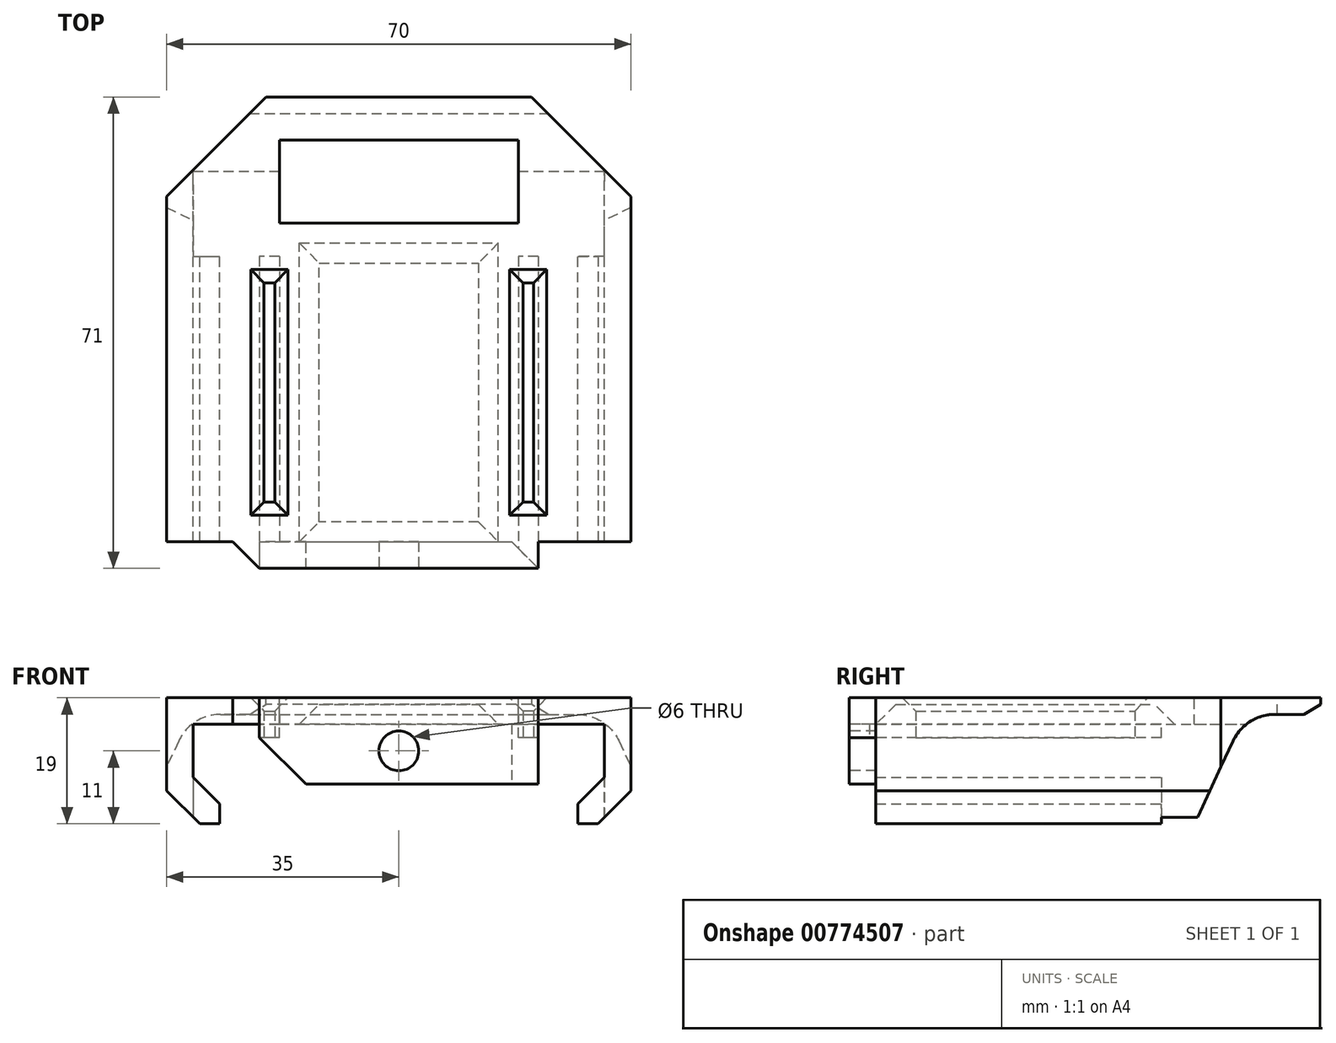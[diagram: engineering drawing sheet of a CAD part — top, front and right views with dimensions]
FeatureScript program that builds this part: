
annotation { "Feature Type Name" : "Feature", "Feature Type Description" : "" }
export const myFeature = defineFeature(function(context is Context, id is Id, definition is map)
    precondition{}
    {
        {
            var Q0;
            Q0=qCreatedBy(makeId("Front.planeOp"),FACE);
            var sketch = newSketch(context, id + "F0", { "sketchPlane" : qUnion([Q0])});
            skLineSegment(sketch, "E0.bottom", {"start": v(-35, 0) * mm, "end": v(35, 0) * mm});
            skLineSegment(sketch, "E0.top", {"start": v(-35, -19) * mm, "end": v(-27, -19) * mm});
            skLineSegment(sketch, "E0.left", {"start": v(-35, 0) * mm, "end": v(-35, -19) * mm});
            skLineSegment(sketch, "E0.right", {"start": v(35, 0) * mm, "end": v(35, -19) * mm});
            skLineSegment(sketch, "E1", {"start": v(-27, -19) * mm, "end": v(-27, -16) * mm});
            skLineSegment(sketch, "E2", {"start": v(-31, -12) * mm, "end": v(-31, -4) * mm});
            skLineSegment(sketch, "E3", {"start": v(-31, -4) * mm, "end": v(31, -4) * mm});
            skLineSegment(sketch, "E4", {"start": v(31, -4) * mm, "end": v(31, -12) * mm});
            skLineSegment(sketch, "E5", {"start": v(27, -16) * mm, "end": v(27, -19) * mm});
            skLineSegment(sketch, "E6.trimOffspring", {"start": v(27, -19) * mm, "end": v(35, -19) * mm});
            skPoint(sketch, "E7.startSnap0", {"position": v(-29, -12) * mm});
            skLineSegment(sketch, "E8", {"start": v(-31, -12) * mm, "end": v(-27, -16) * mm});
            skLineSegment(sketch, "E9", {"start": v(31, -12) * mm, "end": v(27, -16) * mm});
            skPoint(sketch, "E10.orphan", {"position": v(-27, -12) * mm});
            skSolve(sketch);
        }
        {
            var Q0;
            Q0 = qSketchRegion(id + "F0", true);
            extrude(context, id + "F1", {"entities" : qUnion([Q0]), "depth" : 67 * mm, "offsetDistance" : 25 * mm});
        }
        {
            var Q0;
            Q0=makeQuery(id+"F1.opExtrude","SWEPT_FACE",FACE,{"disambiguationData":[OSD([sQuery(id+"F0.wireOp",EDGE,"E0.right")])]});
            var sketch = newSketch(context, id + "F2", { "sketchPlane" : qUnion([Q0])});
            skLineSegment(sketch, "E11.0.1", {"start": v(0, -4) * mm, "end": v(-67, -4) * mm, "construction": true});
            skLineSegment(sketch, "E11.0.3", {"start": v(-67, -4) * mm, "end": v(0, -4) * mm, "construction": true});
            skLineSegment(sketch, "E12", {"start": v(-19, -19) * mm, "end": v(-13.2, -6.54) * mm});
            skLineSegment(sketch, "E13", {"start": v(-6.85, -2.5) * mm, "end": v(4.14, -2.5) * mm});
            skLineSegment(sketch, "E14", {"start": v(4.14, -2.5) * mm, "end": v(4.14, -19) * mm});
            skLineSegment(sketch, "E15", {"start": v(4.14, -19) * mm, "end": v(-19, -19) * mm});
            skPoint(sketch, "E16.visualSharp", {"position": v(-11.3, -2.5) * mm});
            skArc(sketch, "E16.filletArc", {"start": v(-6.85, -2.5) * mm, "mid": v(-10.6, -3.6) * mm, "end": v(-13.2, -6.54) * mm});
            skSolve(sketch);
        }
        {
            var Q0;
            Q0 = qSketchRegion(id + "F2", true);
            extrude(context, id + "F3", {"entities" : qUnion([Q0]), "operationType" : NewBodyOperationType.REMOVE, "endBound" : BoundingType.THROUGH_ALL, "oppositeDirection" : true, "depth" : 25 * mm, "offsetDistance" : 25 * mm});
        }
        {
            var Q0;
            Q0=makeQuery(id+"F1.opExtrude","SWEPT_FACE",FACE,{"disambiguationData":[OSD([sQuery(id+"F0.wireOp",EDGE,"E0.bottom")])]});
            var sketch = newSketch(context, id + "F4", { "sketchPlane" : qUnion([Q0])});
            skLineSegment(sketch, "E17.bottom", {"start": v(18, -19) * mm, "end": v(-18, -19) * mm});
            skLineSegment(sketch, "E17.top", {"start": v(18, -6.5) * mm, "end": v(-18, -6.5) * mm});
            skLineSegment(sketch, "E17.left", {"start": v(18, -19) * mm, "end": v(18, -6.5) * mm});
            skLineSegment(sketch, "E17.right", {"start": v(-18, -19) * mm, "end": v(-18, -6.5) * mm});
            skPoint(sketch, "E17.middle", {"position": v(0, -12.75) * mm});
            skSolve(sketch);
        }
        {
            var Q0;
            Q0 = qSketchRegion(id + "F4", true);
            extrude(context, id + "F5", {"entities" : qUnion([Q0]), "operationType" : NewBodyOperationType.REMOVE, "oppositeDirection" : true, "depth" : 25 * mm, "offsetDistance" : 25 * mm});
        }
        {
            var Q0;
            Q0=makeQuery(id+"F1.opExtrude","SWEPT_FACE",FACE,{"disambiguationData":[OSD([sQuery(id+"F0.wireOp",EDGE,"E3")])]});
            var sketch = newSketch(context, id + "F6", { "sketchPlane" : qUnion([Q0])});
            skLineSegment(sketch, "E18.bottom", {"start": v(-18, 24) * mm, "end": v(-21, 24) * mm});
            skLineSegment(sketch, "E18.top", {"start": v(-18, 67) * mm, "end": v(-21, 67) * mm});
            skLineSegment(sketch, "E18.left", {"start": v(-18, 24) * mm, "end": v(-18, 67) * mm});
            skLineSegment(sketch, "E18.right", {"start": v(-21, 24) * mm, "end": v(-21, 67) * mm});
            skPoint(sketch, "E18.middle", {"position": v(-19.5, 45.5) * mm});
            skLineSegment(sketch, "E19.bottom", {"start": v(21, 24) * mm, "end": v(18, 24) * mm});
            skLineSegment(sketch, "E19.top", {"start": v(21, 67) * mm, "end": v(18, 67) * mm});
            skLineSegment(sketch, "E19.left", {"start": v(21, 24) * mm, "end": v(21, 67) * mm});
            skLineSegment(sketch, "E19.right", {"start": v(18, 24) * mm, "end": v(18, 67) * mm});
            skPoint(sketch, "E19.middle", {"position": v(19.5, 45.5) * mm});
            skSolve(sketch);
        }
        {
            var Q0;
            Q0 = qSketchRegion(id + "F6", true);
            extrude(context, id + "F7", {"entities" : qUnion([Q0]), "operationType" : NewBodyOperationType.ADD, "depth" : 2 * mm, "offsetDistance" : 25 * mm});
        }
        {
            var Q0;
            Q0=makeQuery(id+"F7.opExtrude","CAP_FACE",FACE,{"disambiguationData":[OSD([sQuery(id+"F6.wireOp",EDGE,"E18.bottom"),sQuery(id+"F6.wireOp",EDGE,"E18.top"),sQuery(id+"F6.wireOp",EDGE,"E18.left"),sQuery(id+"F6.wireOp",EDGE,"E18.right")])],"isStart":false});
            var sketch = newSketch(context, id + "F8", { "sketchPlane" : qUnion([Q0])});
            skLineSegment(sketch, "E20.bottom", {"start": v(-18.7, 61) * mm, "end": v(-20.3, 61) * mm});
            skLineSegment(sketch, "E20.top", {"start": v(-18.7, 28) * mm, "end": v(-20.3, 28) * mm});
            skLineSegment(sketch, "E20.left", {"start": v(-18.7, 61) * mm, "end": v(-18.7, 28) * mm});
            skLineSegment(sketch, "E20.right", {"start": v(-20.3, 61) * mm, "end": v(-20.3, 28) * mm});
            skPoint(sketch, "E20.middle", {"position": v(-19.5, 44.5) * mm});
            skLineSegment(sketch, "E21.bottom", {"start": v(20.3, 28) * mm, "end": v(18.7, 28) * mm});
            skLineSegment(sketch, "E21.top", {"start": v(20.3, 61) * mm, "end": v(18.7, 61) * mm});
            skLineSegment(sketch, "E21.left", {"start": v(20.3, 28) * mm, "end": v(20.3, 61) * mm});
            skLineSegment(sketch, "E21.right", {"start": v(18.7, 28) * mm, "end": v(18.7, 61) * mm});
            skPoint(sketch, "E21.middle", {"position": v(19.5, 44.5) * mm});
            skSolve(sketch);
        }
        {
            var Q0;
            Q0 = qSketchRegion(id + "F8", true);
            extrude(context, id + "F9", {"entities" : qUnion([Q0]), "operationType" : NewBodyOperationType.REMOVE, "endBound" : BoundingType.THROUGH_ALL, "oppositeDirection" : true, "depth" : 25 * mm, "offsetDistance" : 25 * mm});
        }
        {
            var Q0;
            Q0=makeQuery(id+"F1.opExtrude","SWEPT_FACE",FACE,{"disambiguationData":[OSD([sQuery(id+"F0.wireOp",EDGE,"E0.bottom")])]});
            var sketch = newSketch(context, id + "F10", { "sketchPlane" : qUnion([Q0])});
            skLineSegment(sketch, "E22.0.2", {"start": v(-21, -67) * mm, "end": v(-18, -67) * mm, "construction": true});
            skLineSegment(sketch, "E22.0.4", {"start": v(-18, -67) * mm, "end": v(18, -67) * mm, "construction": true});
            skLineSegment(sketch, "E22.0.6", {"start": v(18, -67) * mm, "end": v(21, -67) * mm, "construction": true});
            skLineSegment(sketch, "E23.top", {"start": v(21, -71) * mm, "end": v(-21, -71) * mm});
            skLineSegment(sketch, "E23.left", {"start": v(21, -67) * mm, "end": v(21, -71) * mm});
            skLineSegment(sketch, "E23.right", {"start": v(-21, -67) * mm, "end": v(-21, -71) * mm});
            skPoint(sketch, "E23.middle", {"position": v(0, -61.25) * mm});
            skPoint(sketch, "E23.bottom.end.orphan", {"position": v(-21, -51.5) * mm});
            skPoint(sketch, "E24.orphan", {"position": v(21, -51.5) * mm});
            skLineSegment(sketch, "E25.trimOffspring", {"start": v(21, -67) * mm, "end": v(-21, -67) * mm});
            skLineSegment(sketch, "E26", {"start": v(-21, -67) * mm, "end": v(21, -67) * mm});
            skSolve(sketch);
        }
        {
            var Q0;
            Q0 = qSketchRegion(id + "F10", true);
            extrude(context, id + "F11", {"entities" : qUnion([Q0]), "operationType" : NewBodyOperationType.ADD, "oppositeDirection" : true, "depth" : 13 * mm, "offsetDistance" : 25 * mm});
        }
        {
            var Q0;
            Q0=makeQuery(id+"F11.opExtrude","SWEPT_FACE",FACE,{"disambiguationData":[OSD([sQuery(id+"F10.wireOp",EDGE,"E23.top")])]});
            var sketch = newSketch(context, id + "F12", { "sketchPlane" : qUnion([Q0])});
            skCircle(sketch, "E27", {"center": v(0, -8) * mm, "radius": 3 * mm});
            skSolve(sketch);
        }
        {
            var Q0;
            Q0=makeQuery(id+"F1.opExtrude","SWEPT_EDGE",EDGE,{"disambiguationData":[OSD([sQuery(id+"F0.wireOp",EDGE,"E0.top"),sQuery(id+"F0.wireOp",EDGE,"E0.left")])]});
            var Q1;
            Q1=makeQuery(id+"F1.opExtrude","SWEPT_EDGE",EDGE,{"disambiguationData":[OSD([sQuery(id+"F0.wireOp",EDGE,"E0.right"),sQuery(id+"F0.wireOp",EDGE,"E6.trimOffspring")])]});
            chamfer(context, id + "F13", {"entities" : qUnion([Q0, Q1]), "width" : 5 * mm, "tangentPropagation" : true});
        }
        {
            var Q0;
            {var subQ0=sQuery(id+"F10.wireOp",EDGE,"E23.right");var subQ1=sQuery(id+"F0.wireOp",EDGE,"E0.bottom");Q0=makeQuery(id+"F11.boolean.opBoolean","SPLIT",EDGE,{"disambiguationData":[topologyDisambiguationEdgeConnected([makeQuery(id+"F7.opExtrude","SWEPT_FACE",FACE,{"disambiguationData":[OSD([sQuery(id+"F6.wireOp",EDGE,"E18.top")])]})])],"derivedFrom":makeQuery(id+"F11.opExtrude","SWEPT_EDGE",EDGE,{"disambiguationData":[OSD([subQ1,subQ0,sQuery(id+"F10.wireOp",EDGE,"E26")])]})});}
            var Q1;
            {var subQ0=sQuery(id+"F0.wireOp",EDGE,"E0.bottom");var subQ1=sQuery(id+"F10.wireOp",EDGE,"E23.left");Q1=makeQuery(id+"F11.boolean.opBoolean","SPLIT",EDGE,{"disambiguationData":[topologyDisambiguationEdgeConnected([makeQuery(id+"F7.opExtrude","SWEPT_FACE",FACE,{"disambiguationData":[OSD([sQuery(id+"F6.wireOp",EDGE,"E18.top")])]})])],"derivedFrom":makeQuery(id+"F11.opExtrude","SWEPT_EDGE",EDGE,{"disambiguationData":[OSD([subQ0,subQ1,sQuery(id+"F10.wireOp",EDGE,"E26")])]})});}
            chamfer(context, id + "F14", {"entities" : qUnion([Q0, Q1]), "width" : 4 * mm, "tangentPropagation" : true});
        }
        {
            var Q0;
            Q0=makeQuery(id+"F1.opExtrude","CAP_EDGE",EDGE,{"disambiguationData":[OSD([sQuery(id+"F0.wireOp",EDGE,"E0.right")])],"isStart":true});
            var Q1;
            Q1=makeQuery(id+"F1.opExtrude","CAP_EDGE",EDGE,{"disambiguationData":[OSD([sQuery(id+"F0.wireOp",EDGE,"E0.left")])],"isStart":true});
            chamfer(context, id + "F15", {"entities" : qUnion([Q0, Q1]), "width" : 15 * mm, "tangentPropagation" : true});
        }
        {
            var Q0;
            Q0=makeQuery(id+"F11.opExtrude","CAP_EDGE",EDGE,{"disambiguationData":[OSD([sQuery(id+"F10.wireOp",EDGE,"E23.right")])],"isStart":false});
            var Q1;
            Q1=makeQuery(id+"F11.opExtrude","CAP_EDGE",EDGE,{"disambiguationData":[OSD([sQuery(id+"F10.wireOp",EDGE,"E23.left")])],"isStart":false});
            chamfer(context, id + "F16", {"entities" : qUnion([Q0, Q1]), "width" : 7 * mm, "tangentPropagation" : true});
        }
        {
            var Q0;
            Q0 = qSketchRegion(id + "F12", true);
            extrude(context, id + "F17", {"entities" : qUnion([Q0]), "operationType" : NewBodyOperationType.REMOVE, "endBound" : BoundingType.THROUGH_ALL, "oppositeDirection" : true, "depth" : 25 * mm, "offsetDistance" : 25 * mm});
        }
        {
            var Q0;
            Q0=makeQuery(id+"F1.opExtrude","SWEPT_FACE",FACE,{"disambiguationData":[OSD([sQuery(id+"F0.wireOp",EDGE,"E3")])]});
            var sketch = newSketch(context, id + "F18", { "sketchPlane" : qUnion([Q0])});
            skLineSegment(sketch, "E28.bottom", {"start": v(-15, 67) * mm, "end": v(15, 67) * mm});
            skLineSegment(sketch, "E28.top", {"start": v(-15, 22) * mm, "end": v(15, 22) * mm});
            skLineSegment(sketch, "E28.left", {"start": v(-15, 67) * mm, "end": v(-15, 22) * mm});
            skLineSegment(sketch, "E28.right", {"start": v(15, 67) * mm, "end": v(15, 22) * mm});
            skSolve(sketch);
        }
        {
            var Q0;
            Q0 = qSketchRegion(id + "F18", true);
            extrude(context, id + "F19", {"entities" : qUnion([Q0]), "operationType" : NewBodyOperationType.REMOVE, "oppositeDirection" : true, "depth" : 3 * mm, "offsetDistance" : 25 * mm});
        }
        {
            var Q0;
            Q0=makeQuery(id+"F19.boolean.opBoolean","COPY",FACE,{"derivedFrom":makeQuery(id+"F19.opExtrude","CAP_FACE",FACE,{"disambiguationData":[OSD([sQuery(id+"F18.wireOp",EDGE,"E28.bottom"),sQuery(id+"F18.wireOp",EDGE,"E28.top"),sQuery(id+"F18.wireOp",EDGE,"E28.left"),sQuery(id+"F18.wireOp",EDGE,"E28.right")])],"isStart":false})});
            chamfer(context, id + "F20", {"entities" : qUnion([Q0]), "width" : 3 * mm, "tangentPropagation" : true});
        }
        {
            var Q0;
            Q0=makeQuery(id+"F9.boolean.opBoolean","INTERSECT",EDGE,{"derivedFrom":[makeQuery(id+"F1.opExtrude","SWEPT_FACE",FACE,{"disambiguationData":[OSD([sQuery(id+"F0.wireOp",EDGE,"E0.bottom")])]}),makeQuery(id+"F9.opExtrude","SWEPT_FACE",FACE,{"disambiguationData":[OSD([sQuery(id+"F8.wireOp",EDGE,"E21.left")])]})]});
            var Q1;
            Q1=makeQuery(id+"F9.boolean.opBoolean","INTERSECT",EDGE,{"derivedFrom":[makeQuery(id+"F1.opExtrude","SWEPT_FACE",FACE,{"disambiguationData":[OSD([sQuery(id+"F0.wireOp",EDGE,"E0.bottom")])]}),makeQuery(id+"F9.opExtrude","SWEPT_FACE",FACE,{"disambiguationData":[OSD([sQuery(id+"F8.wireOp",EDGE,"E21.right")])]})]});
            var Q2;
            Q2=makeQuery(id+"F9.boolean.opBoolean","INTERSECT",EDGE,{"derivedFrom":[makeQuery(id+"F1.opExtrude","SWEPT_FACE",FACE,{"disambiguationData":[OSD([sQuery(id+"F0.wireOp",EDGE,"E0.bottom")])]}),makeQuery(id+"F9.opExtrude","SWEPT_FACE",FACE,{"disambiguationData":[OSD([sQuery(id+"F8.wireOp",EDGE,"E21.bottom")])]})]});
            var Q3;
            Q3=makeQuery(id+"F9.boolean.opBoolean","INTERSECT",EDGE,{"derivedFrom":[makeQuery(id+"F1.opExtrude","SWEPT_FACE",FACE,{"disambiguationData":[OSD([sQuery(id+"F0.wireOp",EDGE,"E0.bottom")])]}),makeQuery(id+"F9.opExtrude","SWEPT_FACE",FACE,{"disambiguationData":[OSD([sQuery(id+"F8.wireOp",EDGE,"E21.top")])]})]});
            var Q4;
            Q4=makeQuery(id+"F9.boolean.opBoolean","INTERSECT",EDGE,{"derivedFrom":[makeQuery(id+"F1.opExtrude","SWEPT_FACE",FACE,{"disambiguationData":[OSD([sQuery(id+"F0.wireOp",EDGE,"E0.bottom")])]}),makeQuery(id+"F9.opExtrude","SWEPT_FACE",FACE,{"disambiguationData":[OSD([sQuery(id+"F8.wireOp",EDGE,"E20.left")])]})]});
            var Q5;
            Q5=makeQuery(id+"F9.boolean.opBoolean","INTERSECT",EDGE,{"derivedFrom":[makeQuery(id+"F1.opExtrude","SWEPT_FACE",FACE,{"disambiguationData":[OSD([sQuery(id+"F0.wireOp",EDGE,"E0.bottom")])]}),makeQuery(id+"F9.opExtrude","SWEPT_FACE",FACE,{"disambiguationData":[OSD([sQuery(id+"F8.wireOp",EDGE,"E20.top")])]})]});
            var Q6;
            Q6=makeQuery(id+"F9.boolean.opBoolean","INTERSECT",EDGE,{"derivedFrom":[makeQuery(id+"F1.opExtrude","SWEPT_FACE",FACE,{"disambiguationData":[OSD([sQuery(id+"F0.wireOp",EDGE,"E0.bottom")])]}),makeQuery(id+"F9.opExtrude","SWEPT_FACE",FACE,{"disambiguationData":[OSD([sQuery(id+"F8.wireOp",EDGE,"E20.bottom")])]})]});
            var Q7;
            Q7=makeQuery(id+"F9.boolean.opBoolean","INTERSECT",EDGE,{"derivedFrom":[makeQuery(id+"F1.opExtrude","SWEPT_FACE",FACE,{"disambiguationData":[OSD([sQuery(id+"F0.wireOp",EDGE,"E0.bottom")])]}),makeQuery(id+"F9.opExtrude","SWEPT_FACE",FACE,{"disambiguationData":[OSD([sQuery(id+"F8.wireOp",EDGE,"E20.right")])]})]});
            chamfer(context, id + "F21", {"entities" : qUnion([Q0, Q1, Q2, Q3, Q4, Q5, Q6, Q7]), "width" : 2 * mm, "tangentPropagation" : true});
        }
        {
            var Q0;
            Q0=makeQuery(id+"F3.boolean.opBoolean","INTERSECT",EDGE,{"derivedFrom":[makeQuery(id+"F1.opExtrude","CAP_FACE",FACE,{"disambiguationData":[OSD([sQuery(id+"F0.wireOp",EDGE,"E0.bottom"),sQuery(id+"F0.wireOp",EDGE,"E0.top"),sQuery(id+"F0.wireOp",EDGE,"E0.left"),sQuery(id+"F0.wireOp",EDGE,"E0.right"),sQuery(id+"F0.wireOp",EDGE,"E1"),sQuery(id+"F0.wireOp",EDGE,"E2"),sQuery(id+"F0.wireOp",EDGE,"E3"),sQuery(id+"F0.wireOp",EDGE,"E4"),sQuery(id+"F0.wireOp",EDGE,"E5"),sQuery(id+"F0.wireOp",EDGE,"E6.trimOffspring"),sQuery(id+"F0.wireOp",EDGE,"E8"),sQuery(id+"F0.wireOp",EDGE,"E9")])],"isStart":true}),makeQuery(id+"F3.opExtrude","SWEPT_FACE",FACE,{"disambiguationData":[OSD([sQuery(id+"F2.wireOp",EDGE,"E13")])]})]});
            chamfer(context, id + "F22", {"entities" : qUnion([Q0]), "chamferType" : ChamferType.TWO_OFFSETS, "width1" : 2.5 * mm, "oppositeDirection" : false, "width2" : 1.5 * mm, "tangentPropagation" : true});
        }
        {
            var Q0;
            {var subQ0=sQuery(id+"F0.wireOp",EDGE,"E4");var subQ1=sQuery(id+"F0.wireOp",EDGE,"E3");var subQ2=sQuery(id+"F0.wireOp",EDGE,"E0.right");var subQ3=sQuery(id+"F0.wireOp",EDGE,"E0.bottom");var subQ4=sQuery(id+"F0.wireOp",EDGE,"E6.trimOffspring");var subQ6=sQuery(id+"F0.wireOp",EDGE,"E5");var subQ7=sQuery(id+"F0.wireOp",EDGE,"E9");Q0=makeQuery(id+"F11.boolean.opBoolean","SPLIT",FACE,{"disambiguationData":[TD([makeQuery(id+"F1.opExtrude","SWEPT_FACE",FACE,{"disambiguationData":[OSD([subQ2])]})])],"derivedFrom":makeQuery(id+"F7.boolean.opBoolean","MERGE",FACE,{"derivedFrom":[makeQuery(id+"F1.opExtrude","CAP_FACE",FACE,{"disambiguationData":[OSD([subQ3,sQuery(id+"F0.wireOp",EDGE,"E0.top"),sQuery(id+"F0.wireOp",EDGE,"E0.left"),subQ2,sQuery(id+"F0.wireOp",EDGE,"E1"),sQuery(id+"F0.wireOp",EDGE,"E2"),subQ1,subQ0,subQ6,subQ4,sQuery(id+"F0.wireOp",EDGE,"E8"),subQ7])],"isStart":false}),makeQuery(id+"F7.opExtrude","SWEPT_FACE",FACE,{"disambiguationData":[OSD([sQuery(id+"F6.wireOp",EDGE,"E18.top")])]}),makeQuery(id+"F7.opExtrude","SWEPT_FACE",FACE,{"disambiguationData":[OSD([sQuery(id+"F6.wireOp",EDGE,"E19.top")])]})]})});}
            var sketch = newSketch(context, id + "F23", { "sketchPlane" : qUnion([Q0])});
            skLineSegment(sketch, "E29.bottom", {"start": v(-31, -9.28) * mm, "end": v(31, -9.28) * mm});
            skLineSegment(sketch, "E29.top", {"start": v(-31, -26.17) * mm, "end": v(31, -26.17) * mm});
            skLineSegment(sketch, "E29.left", {"start": v(-31, -9.28) * mm, "end": v(-31, -26.17) * mm});
            skLineSegment(sketch, "E29.right", {"start": v(31, -9.28) * mm, "end": v(31, -26.17) * mm});
            skSolve(sketch);
        }
        {
            var Q0;
            Q0 = qSketchRegion(id + "F23", true);
            extrude(context, id + "F24", {"entities" : qUnion([Q0]), "operationType" : NewBodyOperationType.REMOVE, "oppositeDirection" : true, "depth" : 100 * mm, "offsetDistance" : 25 * mm, "hasSecondDirection" : true, "secondDirectionOppositeDirection" : false, "secondDirectionDepth" : -43 * mm});
        }
    });
